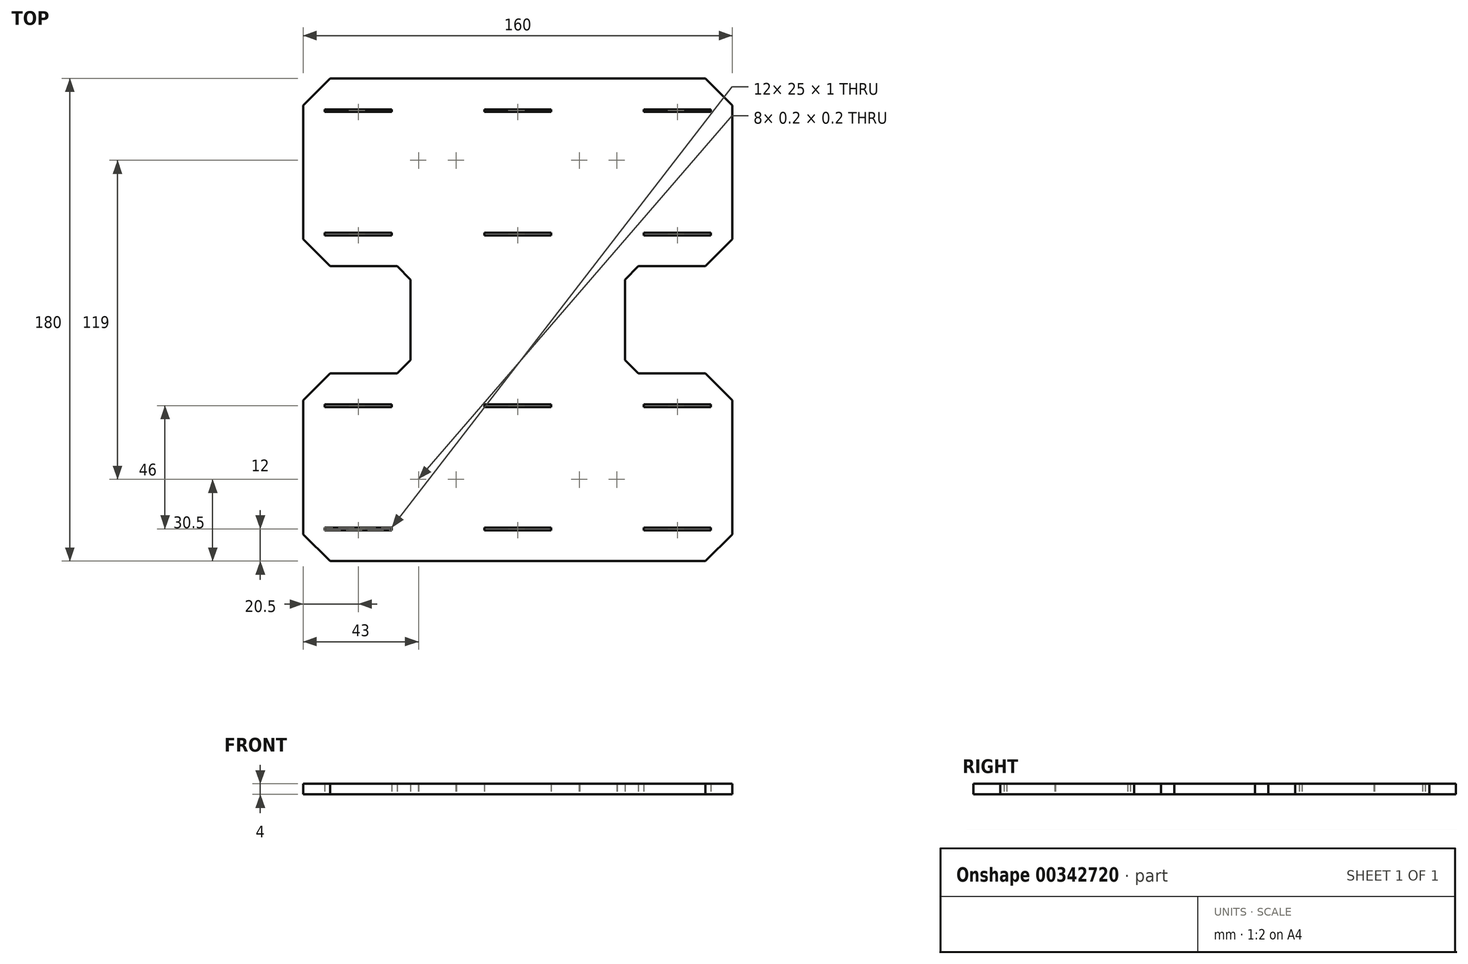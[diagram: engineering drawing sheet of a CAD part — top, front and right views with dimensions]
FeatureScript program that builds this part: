
annotation { "Feature Type Name" : "Feature", "Feature Type Description" : "" }
export const myFeature = defineFeature(function(context is Context, id is Id, definition is map)
    precondition{}
    {
        {
            var Q0;
            Q0=qCreatedBy(makeId("Top.planeOp"),FACE);
            var sketch = newSketch(context, id + "F0", { "sketchPlane" : qUnion([Q0])});
            skLineSegment(sketch, "E0", {"start": v(-233.64, 0) * mm, "end": v(0, 0) * mm, "construction": true});
            skLineSegment(sketch, "E1", {"start": v(0, 90) * mm, "end": v(70, 90) * mm});
            skLineSegment(sketch, "E2", {"start": v(70, 90) * mm, "end": v(80, 80) * mm});
            skLineSegment(sketch, "E3", {"start": v(80, 80) * mm, "end": v(80, 30) * mm});
            skLineSegment(sketch, "E4", {"start": v(80, 30) * mm, "end": v(70, 20) * mm});
            skLineSegment(sketch, "E5", {"start": v(70, 20) * mm, "end": v(45, 20) * mm});
            skLineSegment(sketch, "E6", {"start": v(40, 15) * mm, "end": v(40, 0) * mm});
            skLineSegment(sketch, "E7.bottom", {"start": v(47, 78.5) * mm, "end": v(72, 78.5) * mm});
            skLineSegment(sketch, "E7.top", {"start": v(47, 77.5) * mm, "end": v(72, 77.5) * mm});
            skLineSegment(sketch, "E7.left", {"start": v(47, 78.5) * mm, "end": v(47, 77.5) * mm});
            skLineSegment(sketch, "E7.right", {"start": v(72, 78.5) * mm, "end": v(72, 77.5) * mm});
            skLineSegment(sketch, "E8.bottom", {"start": v(0, 78.5) * mm, "end": v(12.5, 78.5) * mm});
            skLineSegment(sketch, "E8.top", {"start": v(0, 77.5) * mm, "end": v(12.5, 77.5) * mm});
            skLineSegment(sketch, "E8.right", {"start": v(12.5, 78.5) * mm, "end": v(12.5, 77.5) * mm});
            skLineSegment(sketch, "E9", {"start": v(0, 55) * mm, "end": v(80, 55) * mm, "construction": true});
            skLineSegment(sketch, "E10.MirrorCS", {"start": v(12.5, 31.5) * mm, "end": v(12.5, 32.5) * mm});
            skLineSegment(sketch, "E11.MirrorCS", {"start": v(72, 31.5) * mm, "end": v(72, 32.5) * mm});
            skLineSegment(sketch, "E12.MirrorCS", {"start": v(47, 31.5) * mm, "end": v(47, 32.5) * mm});
            skLineSegment(sketch, "E13.MirrorCS", {"start": v(47, 32.5) * mm, "end": v(72, 32.5) * mm});
            skLineSegment(sketch, "E14.MirrorCS", {"start": v(47, 31.5) * mm, "end": v(72, 31.5) * mm});
            skLineSegment(sketch, "E15.MirrorCS", {"start": v(70, 20) * mm, "end": v(80, 30) * mm});
            skLineSegment(sketch, "E16.MirrorCS", {"start": v(0, 31.5) * mm, "end": v(12.5, 31.5) * mm});
            skLineSegment(sketch, "E17.MirrorCS", {"start": v(0, 32.5) * mm, "end": v(12.5, 32.5) * mm});
            skLineSegment(sketch, "E18", {"start": v(0, 106.37) * mm, "end": v(0, 0) * mm, "construction": true});
            skLineSegment(sketch, "E19", {"start": v(0, 78) * mm, "end": v(72, 78) * mm, "construction": true});
            skLineSegment(sketch, "E20", {"start": v(40, 15) * mm, "end": v(45, 20) * mm});
            skLineSegment(sketch, "E21.MirrorCS", {"start": v(0, 78.5) * mm, "end": v(-12.5, 78.5) * mm});
            skLineSegment(sketch, "E22.MirrorCS", {"start": v(-12.5, 78.5) * mm, "end": v(-12.5, 77.5) * mm});
            skLineSegment(sketch, "E23.MirrorCS", {"start": v(0, 77.5) * mm, "end": v(-12.5, 77.5) * mm});
            skLineSegment(sketch, "E24.MirrorCS", {"start": v(0, 78) * mm, "end": v(-72, 78) * mm, "construction": true});
            skLineSegment(sketch, "E25.MirrorCS", {"start": v(-47, 78.5) * mm, "end": v(-47, 77.5) * mm});
            skLineSegment(sketch, "E26.MirrorCS", {"start": v(-47, 78.5) * mm, "end": v(-72, 78.5) * mm});
            skLineSegment(sketch, "E27.MirrorCS", {"start": v(-47, 77.5) * mm, "end": v(-72, 77.5) * mm});
            skLineSegment(sketch, "E28.MirrorCS", {"start": v(-72, 78.5) * mm, "end": v(-72, 77.5) * mm});
            skLineSegment(sketch, "E29.MirrorCS", {"start": v(0, 55) * mm, "end": v(-80, 55) * mm, "construction": true});
            skLineSegment(sketch, "E30.MirrorCS", {"start": v(0, 32.5) * mm, "end": v(-12.5, 32.5) * mm});
            skLineSegment(sketch, "E31.MirrorCS", {"start": v(-12.5, 31.5) * mm, "end": v(-12.5, 32.5) * mm});
            skLineSegment(sketch, "E32.MirrorCS", {"start": v(0, 31.5) * mm, "end": v(-12.5, 31.5) * mm});
            skLineSegment(sketch, "E33.MirrorCS", {"start": v(-47, 31.5) * mm, "end": v(-47, 32.5) * mm});
            skLineSegment(sketch, "E34.MirrorCS", {"start": v(-47, 32.5) * mm, "end": v(-72, 32.5) * mm});
            skLineSegment(sketch, "E35.MirrorCS", {"start": v(-47, 31.5) * mm, "end": v(-72, 31.5) * mm});
            skLineSegment(sketch, "E36.MirrorCS", {"start": v(-72, 31.5) * mm, "end": v(-72, 32.5) * mm});
            skLineSegment(sketch, "E37.MirrorCS", {"start": v(0, 90) * mm, "end": v(-70, 90) * mm});
            skLineSegment(sketch, "E38.MirrorCS", {"start": v(-70, 90) * mm, "end": v(-80, 80) * mm});
            skLineSegment(sketch, "E39.MirrorCS", {"start": v(-80, 80) * mm, "end": v(-80, 30) * mm});
            skLineSegment(sketch, "E40.MirrorCS", {"start": v(-70, 20) * mm, "end": v(-80, 30) * mm});
            skLineSegment(sketch, "E41.MirrorCS", {"start": v(-70, 20) * mm, "end": v(-45, 20) * mm});
            skLineSegment(sketch, "E42.MirrorCS", {"start": v(-40, 15) * mm, "end": v(-45, 20) * mm});
            skLineSegment(sketch, "E43.MirrorCS", {"start": v(-40, 15) * mm, "end": v(-40, 0) * mm});
            skLineSegment(sketch, "E44.MirrorCS", {"start": v(-40, -15) * mm, "end": v(-40, 0) * mm});
            skLineSegment(sketch, "E45.MirrorCS", {"start": v(-40, -15) * mm, "end": v(-45, -20) * mm});
            skLineSegment(sketch, "E46.MirrorCS", {"start": v(-70, -20) * mm, "end": v(-45, -20) * mm});
            skLineSegment(sketch, "E47.MirrorCS", {"start": v(-70, -20) * mm, "end": v(-80, -30) * mm});
            skLineSegment(sketch, "E48.MirrorCS", {"start": v(-80, -80) * mm, "end": v(-80, -30) * mm});
            skLineSegment(sketch, "E49.MirrorCS", {"start": v(-70, -90) * mm, "end": v(-80, -80) * mm});
            skLineSegment(sketch, "E50.MirrorCS", {"start": v(0, -90) * mm, "end": v(-70, -90) * mm});
            skLineSegment(sketch, "E51.MirrorCS", {"start": v(0, -90) * mm, "end": v(70, -90) * mm});
            skLineSegment(sketch, "E52.MirrorCS", {"start": v(70, -90) * mm, "end": v(80, -80) * mm});
            skLineSegment(sketch, "E53.MirrorCS", {"start": v(80, -80) * mm, "end": v(80, -30) * mm});
            skLineSegment(sketch, "E54.MirrorCS", {"start": v(70, -20) * mm, "end": v(80, -30) * mm});
            skLineSegment(sketch, "E55.MirrorCS", {"start": v(70, -20) * mm, "end": v(45, -20) * mm});
            skLineSegment(sketch, "E56.MirrorCS", {"start": v(40, -15) * mm, "end": v(45, -20) * mm});
            skLineSegment(sketch, "E57.MirrorCS", {"start": v(40, -15) * mm, "end": v(40, 0) * mm});
            skLineSegment(sketch, "E58.MirrorCS", {"start": v(-72, -78.5) * mm, "end": v(-72, -77.5) * mm});
            skLineSegment(sketch, "E59.MirrorCS", {"start": v(-47, -78.5) * mm, "end": v(-72, -78.5) * mm});
            skLineSegment(sketch, "E60.MirrorCS", {"start": v(-47, -77.5) * mm, "end": v(-72, -77.5) * mm});
            skLineSegment(sketch, "E61.MirrorCS", {"start": v(-47, -78.5) * mm, "end": v(-47, -77.5) * mm});
            skLineSegment(sketch, "E62.MirrorCS", {"start": v(-72, -31.5) * mm, "end": v(-72, -32.5) * mm});
            skLineSegment(sketch, "E63.MirrorCS", {"start": v(-47, -32.5) * mm, "end": v(-72, -32.5) * mm});
            skLineSegment(sketch, "E64.MirrorCS", {"start": v(-47, -31.5) * mm, "end": v(-72, -31.5) * mm});
            skLineSegment(sketch, "E65.MirrorCS", {"start": v(-47, -31.5) * mm, "end": v(-47, -32.5) * mm});
            skLineSegment(sketch, "E66.MirrorCS", {"start": v(0, -32.5) * mm, "end": v(-12.5, -32.5) * mm});
            skLineSegment(sketch, "E67.MirrorCS", {"start": v(-12.5, -31.5) * mm, "end": v(-12.5, -32.5) * mm});
            skLineSegment(sketch, "E68.MirrorCS", {"start": v(0, -31.5) * mm, "end": v(-12.5, -31.5) * mm});
            skLineSegment(sketch, "E69.MirrorCS", {"start": v(0, -78.5) * mm, "end": v(-12.5, -78.5) * mm});
            skLineSegment(sketch, "E70.MirrorCS", {"start": v(-12.5, -78.5) * mm, "end": v(-12.5, -77.5) * mm});
            skLineSegment(sketch, "E71.MirrorCS", {"start": v(0, -77.5) * mm, "end": v(-12.5, -77.5) * mm});
            skLineSegment(sketch, "E72.MirrorCS", {"start": v(0, -78.5) * mm, "end": v(12.5, -78.5) * mm});
            skLineSegment(sketch, "E73.MirrorCS", {"start": v(12.5, -78.5) * mm, "end": v(12.5, -77.5) * mm});
            skLineSegment(sketch, "E74.MirrorCS", {"start": v(0, -77.5) * mm, "end": v(12.5, -77.5) * mm});
            skLineSegment(sketch, "E75.MirrorCS", {"start": v(47, -78.5) * mm, "end": v(47, -77.5) * mm});
            skLineSegment(sketch, "E76.MirrorCS", {"start": v(47, -78.5) * mm, "end": v(72, -78.5) * mm});
            skLineSegment(sketch, "E77.MirrorCS", {"start": v(72, -78.5) * mm, "end": v(72, -77.5) * mm});
            skLineSegment(sketch, "E78.MirrorCS", {"start": v(47, -77.5) * mm, "end": v(72, -77.5) * mm});
            skLineSegment(sketch, "E79.MirrorCS", {"start": v(0, -32.5) * mm, "end": v(12.5, -32.5) * mm});
            skLineSegment(sketch, "E80.MirrorCS", {"start": v(12.5, -31.5) * mm, "end": v(12.5, -32.5) * mm});
            skLineSegment(sketch, "E81.MirrorCS", {"start": v(0, -31.5) * mm, "end": v(12.5, -31.5) * mm});
            skLineSegment(sketch, "E82.MirrorCS", {"start": v(47, -31.5) * mm, "end": v(47, -32.5) * mm});
            skLineSegment(sketch, "E83.MirrorCS", {"start": v(47, -32.5) * mm, "end": v(72, -32.5) * mm});
            skLineSegment(sketch, "E84.MirrorCS", {"start": v(47, -31.5) * mm, "end": v(72, -31.5) * mm});
            skLineSegment(sketch, "E85.MirrorCS", {"start": v(72, -31.5) * mm, "end": v(72, -32.5) * mm});
            skLineSegment(sketch, "E86.bottom", {"start": v(22.9, 59.6) * mm, "end": v(23.1, 59.6) * mm});
            skLineSegment(sketch, "E86.top", {"start": v(22.9, 59.4) * mm, "end": v(23.1, 59.4) * mm});
            skLineSegment(sketch, "E86.left", {"start": v(22.9, 59.6) * mm, "end": v(22.9, 59.4) * mm});
            skLineSegment(sketch, "E86.right", {"start": v(23.1, 59.6) * mm, "end": v(23.1, 59.4) * mm});
            skLineSegment(sketch, "E87.bottom", {"start": v(36.9, 59.6) * mm, "end": v(37.1, 59.6) * mm});
            skLineSegment(sketch, "E87.top", {"start": v(36.9, 59.4) * mm, "end": v(37.1, 59.4) * mm});
            skLineSegment(sketch, "E87.left", {"start": v(36.9, 59.6) * mm, "end": v(36.9, 59.4) * mm});
            skLineSegment(sketch, "E87.right", {"start": v(37.1, 59.6) * mm, "end": v(37.1, 59.4) * mm});
            skLineSegment(sketch, "E88", {"start": v(22.9, 59.4) * mm, "end": v(23.1, 59.6) * mm, "construction": true});
            skLineSegment(sketch, "E89", {"start": v(23.1, 59.4) * mm, "end": v(22.9, 59.6) * mm, "construction": true});
            skLineSegment(sketch, "E90", {"start": v(36.9, 59.4) * mm, "end": v(37.1, 59.6) * mm, "construction": true});
            skLineSegment(sketch, "E91", {"start": v(37.1, 59.4) * mm, "end": v(36.9, 59.6) * mm, "construction": true});
            skPoint(sketch, "E92", {"position": v(23, 59.5) * mm});
            skPoint(sketch, "E93", {"position": v(37, 59.5) * mm});
            skLineSegment(sketch, "E94.MirrorCS", {"start": v(-36.9, 59.4) * mm, "end": v(-37.1, 59.6) * mm, "construction": true});
            skPoint(sketch, "E95.MirrorP", {"position": v(-23, 59.5) * mm});
            skLineSegment(sketch, "E96.MirrorCS", {"start": v(-37.1, 59.4) * mm, "end": v(-36.9, 59.6) * mm, "construction": true});
            skPoint(sketch, "E97.MirrorP", {"position": v(-37, 59.5) * mm});
            skLineSegment(sketch, "E98.MirrorCS", {"start": v(-36.9, 59.4) * mm, "end": v(-37.1, 59.4) * mm});
            skLineSegment(sketch, "E99.MirrorCS", {"start": v(-37.1, 59.6) * mm, "end": v(-37.1, 59.4) * mm});
            skLineSegment(sketch, "E100.MirrorCS", {"start": v(-36.9, 59.6) * mm, "end": v(-37.1, 59.6) * mm});
            skLineSegment(sketch, "E101.MirrorCS", {"start": v(-22.9, 59.4) * mm, "end": v(-23.1, 59.6) * mm, "construction": true});
            skLineSegment(sketch, "E102.MirrorCS", {"start": v(-23.1, 59.4) * mm, "end": v(-22.9, 59.6) * mm, "construction": true});
            skLineSegment(sketch, "E103.MirrorCS", {"start": v(-22.9, 59.6) * mm, "end": v(-23.1, 59.6) * mm});
            skLineSegment(sketch, "E104.MirrorCS", {"start": v(-22.9, 59.6) * mm, "end": v(-22.9, 59.4) * mm});
            skLineSegment(sketch, "E105.MirrorCS", {"start": v(-36.9, 59.6) * mm, "end": v(-36.9, 59.4) * mm});
            skLineSegment(sketch, "E106.MirrorCS", {"start": v(-22.9, 59.4) * mm, "end": v(-23.1, 59.4) * mm});
            skLineSegment(sketch, "E107.MirrorCS", {"start": v(-23.1, 59.6) * mm, "end": v(-23.1, 59.4) * mm});
            skLineSegment(sketch, "E108.MirrorCS", {"start": v(-22.9, -59.6) * mm, "end": v(-22.9, -59.4) * mm});
            skLineSegment(sketch, "E109.MirrorCS", {"start": v(-22.9, -59.4) * mm, "end": v(-23.1, -59.4) * mm});
            skLineSegment(sketch, "E110.MirrorCS", {"start": v(-23.1, -59.6) * mm, "end": v(-23.1, -59.4) * mm});
            skLineSegment(sketch, "E111.MirrorCS", {"start": v(-22.9, -59.6) * mm, "end": v(-23.1, -59.6) * mm});
            skLineSegment(sketch, "E112.MirrorCS", {"start": v(-23.1, -59.4) * mm, "end": v(-22.9, -59.6) * mm, "construction": true});
            skLineSegment(sketch, "E113.MirrorCS", {"start": v(-22.9, -59.4) * mm, "end": v(-23.1, -59.6) * mm, "construction": true});
            skLineSegment(sketch, "E114.MirrorCS", {"start": v(-36.9, -59.6) * mm, "end": v(-37.1, -59.6) * mm});
            skLineSegment(sketch, "E115.MirrorCS", {"start": v(-37.1, -59.6) * mm, "end": v(-37.1, -59.4) * mm});
            skLineSegment(sketch, "E116.MirrorCS", {"start": v(-36.9, -59.6) * mm, "end": v(-36.9, -59.4) * mm});
            skLineSegment(sketch, "E117.MirrorCS", {"start": v(-36.9, -59.4) * mm, "end": v(-37.1, -59.4) * mm});
            skLineSegment(sketch, "E118.MirrorCS", {"start": v(-37.1, -59.4) * mm, "end": v(-36.9, -59.6) * mm, "construction": true});
            skLineSegment(sketch, "E119.MirrorCS", {"start": v(-36.9, -59.4) * mm, "end": v(-37.1, -59.6) * mm, "construction": true});
            skPoint(sketch, "E120.MirrorP", {"position": v(-23, -59.5) * mm});
            skPoint(sketch, "E121.MirrorP", {"position": v(-37, -59.5) * mm});
            skLineSegment(sketch, "E122.MirrorCS", {"start": v(36.9, -59.4) * mm, "end": v(37.1, -59.4) * mm});
            skLineSegment(sketch, "E123.MirrorCS", {"start": v(36.9, -59.6) * mm, "end": v(37.1, -59.6) * mm});
            skLineSegment(sketch, "E124.MirrorCS", {"start": v(37.1, -59.6) * mm, "end": v(37.1, -59.4) * mm});
            skLineSegment(sketch, "E125.MirrorCS", {"start": v(36.9, -59.6) * mm, "end": v(36.9, -59.4) * mm});
            skLineSegment(sketch, "E126.MirrorCS", {"start": v(37.1, -59.4) * mm, "end": v(36.9, -59.6) * mm, "construction": true});
            skLineSegment(sketch, "E127.MirrorCS", {"start": v(36.9, -59.4) * mm, "end": v(37.1, -59.6) * mm, "construction": true});
            skLineSegment(sketch, "E128.MirrorCS", {"start": v(22.9, -59.6) * mm, "end": v(23.1, -59.6) * mm});
            skLineSegment(sketch, "E129.MirrorCS", {"start": v(22.9, -59.6) * mm, "end": v(22.9, -59.4) * mm});
            skLineSegment(sketch, "E130.MirrorCS", {"start": v(22.9, -59.4) * mm, "end": v(23.1, -59.6) * mm, "construction": true});
            skLineSegment(sketch, "E131.MirrorCS", {"start": v(22.9, -59.4) * mm, "end": v(23.1, -59.4) * mm});
            skLineSegment(sketch, "E132.MirrorCS", {"start": v(23.1, -59.4) * mm, "end": v(22.9, -59.6) * mm, "construction": true});
            skLineSegment(sketch, "E133.MirrorCS", {"start": v(23.1, -59.6) * mm, "end": v(23.1, -59.4) * mm});
            skPoint(sketch, "E134.MirrorP", {"position": v(37, -59.5) * mm});
            skPoint(sketch, "E135.MirrorP", {"position": v(23, -59.5) * mm});
            skSolve(sketch);
        }
        {
            var Q0;
            {var subQ2=sQuery(id+"F0.wireOp",EDGE,"E1");Q0=makeQuery(id+"F0.imprint","IMPRINT",FACE,{"disambiguationData":[TD([[makeQuery(id+"F0.imprint","IMPRINT",EDGE,{"derivedFrom":subQ2}),-1.0]])]});}
            extrude(context, id + "F1", {"entities" : qUnion([Q0]), "depth" : 4 * mm});
        }
    });
